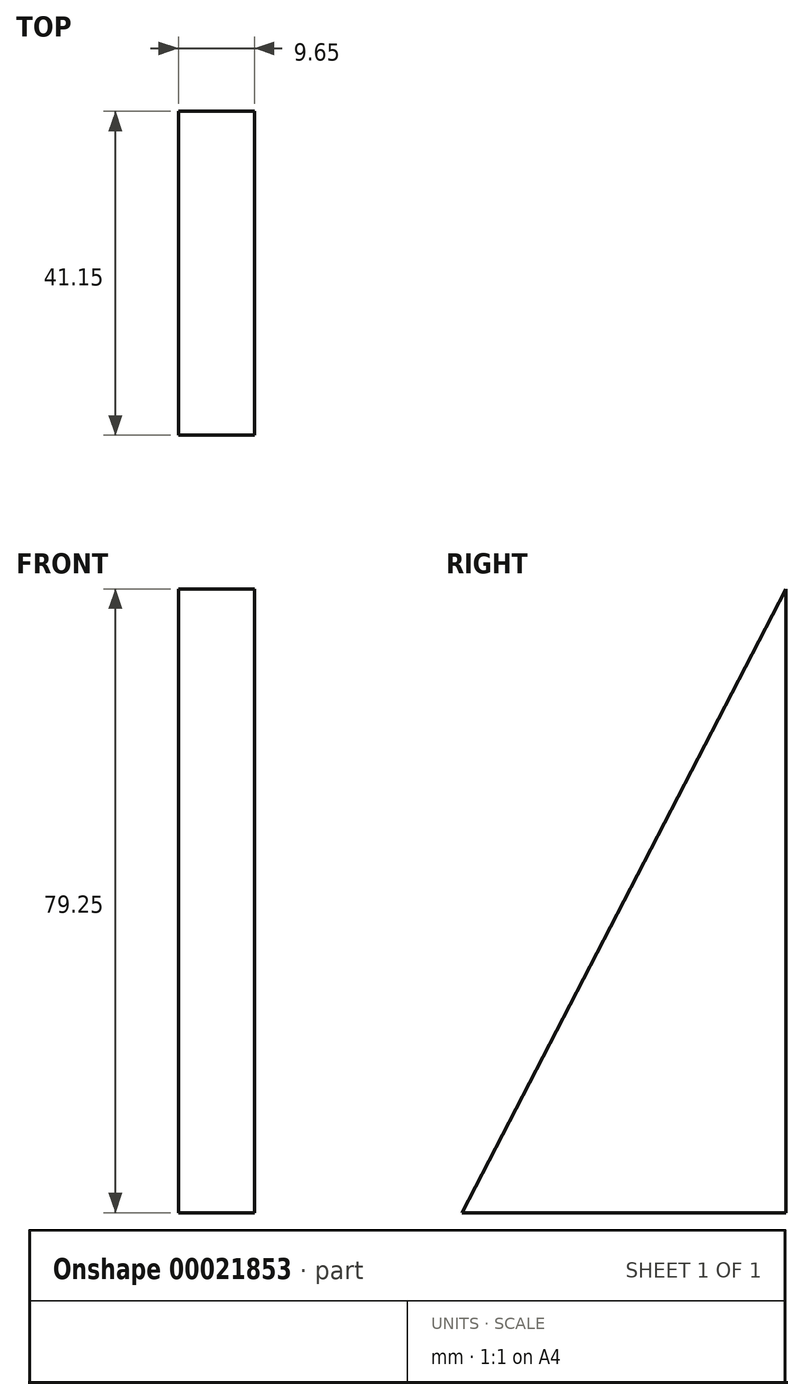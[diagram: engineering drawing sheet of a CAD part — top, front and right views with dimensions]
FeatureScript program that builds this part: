
annotation { "Feature Type Name" : "Feature", "Feature Type Description" : "" }
export const myFeature = defineFeature(function(context is Context, id is Id, definition is map)
    precondition{}
    {
        {
            var Q0;
            Q0=qCreatedBy(makeId("Right.planeOp"),FACE);
            var sketch = newSketch(context, id + "F0", { "sketchPlane" : qUnion([Q0])});
            skLineSegment(sketch, "E0.top", {"start": v(-24.06, -27.6) * mm, "end": v(17.1, -27.6) * mm});
            skLineSegment(sketch, "E0.right", {"start": v(17.1, 51.64) * mm, "end": v(17.1, -27.6) * mm});
            skLineSegment(sketch, "E1", {"start": v(17.1, 51.64) * mm, "end": v(-24.06, -27.6) * mm});
            skSolve(sketch);
        }
        {
            var Q0;
            Q0 = qSketchRegion(id + "F0", true);
            extrude(context, id + "F1", {"entities" : qUnion([Q0]), "depth" : 9.65 * mm});
        }
    });
